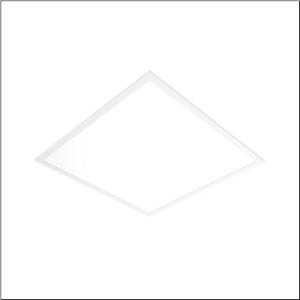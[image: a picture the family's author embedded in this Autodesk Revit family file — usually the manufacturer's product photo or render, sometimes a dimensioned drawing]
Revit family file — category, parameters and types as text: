
# Revit family: apollon_41_51mh12wd2m43
name_source: partatom
category: Lighting Fixtures
units: mm (PartAtom-declared; Revit-internal decimal feet)

## family parameters
Cut with Voids When Loaded = No
Host = Face
Light Source = No
Part Type = Normal
Room Calculation Point = No
Round Connector Dimension = Use Diameter
Shared = No

## types (1)
- --- (1 x LED, 530 lm, 4.9 W, 4000K)
    Apparent Load = 5 VA
    CIE Flux Codes = 61 87 97 100 100
    Color Rendering = 80
    Color Temperature = 4000K
    Default Elevation = 1800 mm
    Description = Apollon 41, office luminaire, primary optical cover: prismatic diffuser, of PS, light emission: direct distribution, primary light characteristic: symmetric, installation type: lay-in mounting, LED, rated luminous flux: 3.500lm, luminous efficacy: 123lm/W, light colour: 830/840, colour temperature: 3000/4000K, control gear: DALI 2, with terminal, 5-pole, mains connection: 220..240V, AC/DC, 0/50..60Hz, suitable for self-contained emergency lighting element 58DB00B013A with integrated self-test function according to EN 60598-2-22, housing, of aluminium section, traffic white (RAL 9016), module: M600, length: 595mm, width: 595mm, height: 60mm, recess depth: 180mm, housing upper side, of sheet steel, protection rating (complete): IP20, protection rating (lamp compartment, on room side): IP40, insulation class (complete): insulation class II (safety insulation), certification: CE, ENEC, impact resistance: IK03, permissible operating ambient temperature: -25..+40°C, packaging unit: 1 piece
    Height = 0 mm  [stored 0 ft]
    Lamp = 1 x LED
    Lamp Light Flux = 530 lm
    Lamp Power = 4.9 W
    Lamp count = 1
    Length = 595 mm
    Luminous efficacy = 108 lm/W
    Manufacturer = Siteco
    ModVariant = No
    Model = 51MH12WD2M43
    Mounting Place = Ceiling
    Mounting Type = Recessed
    Number of Poles = 1
    OnlyDefault = Yes
    Power Factor = 1
    Product Name = Apollon 41
    Product group = office luminaire | ceiling recessed
    ProductGroupID = 400
    Protection Class = Protection class II
    Protection Degree = IP 20
    RLX_Detail_Level = 1
    RLX_Emergency_Light_Flux = 0 lm
    RLX_Emergency_Type = 0
    RLX_Emergency_Type_DB = No
    RlxData = <blob elided: 12901 chars, md5=b3039059>
    Socket = socket
    Standby Power = 0 W
    System Light Flux = 530 lm
    System Power = 5 W
    Type Comments = : DC mode (central or group accumulator) initial emergency light level
    Type Image = l_1291024.jpg
    URL = http://relux.com
    VarID = @adj_000001
    Voltage = 0 V
    Weight = 0.00 kg
    Width = 595 mm

note: [stored X ft] marks values corroborated as IEEE doubles in the binary element streams (Revit-internal decimal feet)

## geometry (parser evidence)
native form markers: Sweep x10
no freeform markers — native parametric forms only
